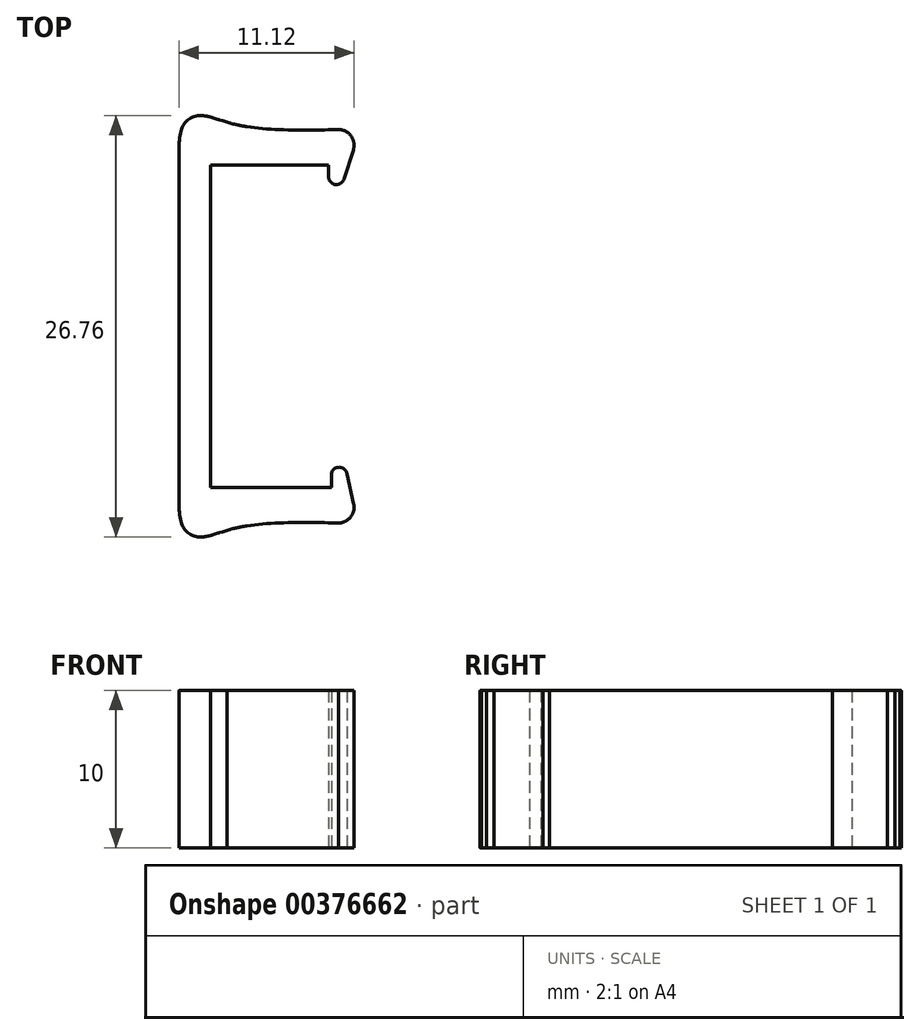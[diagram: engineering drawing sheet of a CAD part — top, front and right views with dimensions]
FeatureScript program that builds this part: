
annotation { "Feature Type Name" : "Feature", "Feature Type Description" : "" }
export const myFeature = defineFeature(function(context is Context, id is Id, definition is map)
    precondition{}
    {
        {
            var Q0;
            Q0=qCreatedBy(makeId("Top.planeOp"),FACE);
            var sketch = newSketch(context, id + "F0", { "sketchPlane" : qUnion([Q0])});
            skLineSegment(sketch, "E0.right", {"start": v(-6, 11) * mm, "end": v(-6, -11) * mm});
            skLineSegment(sketch, "E1.2", {"start": v(3.68, -10.25) * mm, "end": v(-4, -10.25) * mm});
            skLineSegment(sketch, "E1.3", {"start": v(-4, 10.25) * mm, "end": v(-4, -10.25) * mm});
            skLineSegment(sketch, "E2", {"start": v(3.5, 10.25) * mm, "end": v(3.5, 9.5) * mm});
            skArc(sketch, "E3.filletArc", {"start": v(3.5, 9.5) * mm, "mid": v(3.92, 9) * mm, "end": v(4.48, 9.35) * mm});
            skLineSegment(sketch, "E4", {"start": v(4.48, 9.35) * mm, "end": v(5.07, 11.2) * mm});
            skLineSegment(sketch, "E5.trimOffspring", {"start": v(3.5, 10.25) * mm, "end": v(-4, 10.25) * mm});
            skArc(sketch, "E6.MirrorCS", {"start": v(3.68, -9.5) * mm, "mid": v(4.12, -8.96) * mm, "end": v(4.68, -9.39) * mm});
            skLineSegment(sketch, "E7.MirrorCS", {"start": v(3.68, -10.25) * mm, "end": v(3.68, -9.5) * mm});
            skLineSegment(sketch, "E8.MirrorCS", {"start": v(4.68, -9.39) * mm, "end": v(5.1, -11.28) * mm});
            skPoint(sketch, "E9.visualSharp", {"position": v(5.37, -12.5) * mm});
            skArc(sketch, "E9.filletArc", {"start": v(4.12, -12.5) * mm, "mid": v(4.9, -12.13) * mm, "end": v(5.1, -11.28) * mm});
            skPoint(sketch, "E10.visualSharp", {"position": v(5.5, 12.5) * mm});
            skArc(sketch, "E10.filletArc", {"start": v(5.07, 11.2) * mm, "mid": v(4.93, 12.09) * mm, "end": v(4.12, 12.5) * mm});
            skPoint(sketch, "E11.visualSharp", {"position": v(-6, 12.5) * mm});
            skPoint(sketch, "E12.visualSharp", {"position": v(-6, -12.5) * mm});
            skLineSegment(sketch, "E13", {"start": v(-4, 10.25) * mm, "end": v(3.68, -10.25) * mm, "construction": true});
            skLineSegment(sketch, "E14", {"start": v(3.5, 10.25) * mm, "end": v(-4, -10.25) * mm, "construction": true});
            skLineSegment(sketch, "E15", {"start": v(0, 0) * mm, "end": v(7.63, 0) * mm, "construction": true});
            skFitSpline(sketch, "E16", {"points": [v(-6, 11) * mm, v(-5.67, 12.86) * mm, v(-4.63, 13.38) * mm, v(-2.08, 12.75) * mm, v(4.12, 12.5) * mm], "startDerivative": vector(0.04, 10.94) * mm, "endDerivative": vector(13.03, 0.4) * mm});
            skArc(sketch, "E17", {"start": v(-4.58, 13.38) * mm, "mid": v(-4.63, 13.43) * mm, "end": v(-4.68, 13.38) * mm});
            skArc(sketch, "E18", {"start": v(-4.28, 13.35) * mm, "mid": v(-4.32, 13.4) * mm, "end": v(-4.38, 13.37) * mm});
            skArc(sketch, "E19", {"start": v(-3.99, 13.29) * mm, "mid": v(-4.02, 13.35) * mm, "end": v(-4.08, 13.31) * mm});
            skArc(sketch, "E20", {"start": v(-3.7, 13.2) * mm, "mid": v(-3.73, 13.26) * mm, "end": v(-3.8, 13.23) * mm});
            skArc(sketch, "E21", {"start": v(-3.41, 13.11) * mm, "mid": v(-3.45, 13.17) * mm, "end": v(-3.5, 13.14) * mm});
            skArc(sketch, "E22", {"start": v(-3.13, 13.02) * mm, "mid": v(-3.16, 13.08) * mm, "end": v(-3.22, 13.05) * mm});
            skArc(sketch, "E23", {"start": v(-2.84, 12.94) * mm, "mid": v(-2.87, 13) * mm, "end": v(-2.94, 12.96) * mm});
            skArc(sketch, "E24", {"start": v(-2.55, 12.86) * mm, "mid": v(-2.59, 12.92) * mm, "end": v(-2.65, 12.88) * mm});
            skArc(sketch, "E25", {"start": v(-2.26, 12.79) * mm, "mid": v(-2.3, 12.85) * mm, "end": v(-2.36, 12.8) * mm});
            skArc(sketch, "E26", {"start": v(-1.96, 12.73) * mm, "mid": v(-2, 12.79) * mm, "end": v(-2.06, 12.75) * mm});
            skArc(sketch, "E27", {"start": v(-1.66, 12.68) * mm, "mid": v(-1.7, 12.73) * mm, "end": v(-1.76, 12.7) * mm});
            skArc(sketch, "E28.MirrorCS", {"start": v(-1.96, -12.73) * mm, "mid": v(-2, -12.79) * mm, "end": v(-2.06, -12.75) * mm});
            skArc(sketch, "E29.MirrorCS", {"start": v(-2.26, -12.79) * mm, "mid": v(-2.3, -12.85) * mm, "end": v(-2.36, -12.8) * mm});
            skFitSpline(sketch, "E30.MirrorCS", {"points": [v(-6, -11) * mm, v(-5.67, -12.86) * mm, v(-4.63, -13.38) * mm, v(-2.08, -12.75) * mm, v(4.12, -12.5) * mm], "startDerivative": vector(0.04, -10.94) * mm, "endDerivative": vector(13.03, -0.4) * mm});
            skArc(sketch, "E31.MirrorCS", {"start": v(-1.66, -12.68) * mm, "mid": v(-1.7, -12.73) * mm, "end": v(-1.76, -12.7) * mm});
            skArc(sketch, "E32.MirrorCS", {"start": v(-4.58, -13.38) * mm, "mid": v(-4.63, -13.43) * mm, "end": v(-4.68, -13.38) * mm});
            skArc(sketch, "E33.MirrorCS", {"start": v(-4.28, -13.35) * mm, "mid": v(-4.32, -13.4) * mm, "end": v(-4.38, -13.37) * mm});
            skFitSpline(sketch, "E34.MirrorCS", {"points": [v(-6, -11) * mm, v(-5.67, -12.86) * mm, v(-4.63, -13.38) * mm, v(-2.08, -12.75) * mm, v(4.12, -12.5) * mm], "startDerivative": vector(0.04, -10.94) * mm, "endDerivative": vector(13.03, -0.4) * mm});
            skArc(sketch, "E35.MirrorCS", {"start": v(-3.99, -13.29) * mm, "mid": v(-4.02, -13.35) * mm, "end": v(-4.08, -13.31) * mm});
            skArc(sketch, "E36.MirrorCS", {"start": v(-2.55, -12.86) * mm, "mid": v(-2.59, -12.92) * mm, "end": v(-2.65, -12.88) * mm});
            skArc(sketch, "E37.MirrorCS", {"start": v(-2.84, -12.94) * mm, "mid": v(-2.87, -13) * mm, "end": v(-2.94, -12.96) * mm});
            skArc(sketch, "E38.MirrorCS", {"start": v(-3.7, -13.2) * mm, "mid": v(-3.73, -13.26) * mm, "end": v(-3.8, -13.23) * mm});
            skArc(sketch, "E39.MirrorCS", {"start": v(-3.13, -13.02) * mm, "mid": v(-3.16, -13.08) * mm, "end": v(-3.22, -13.05) * mm});
            skArc(sketch, "E40.MirrorCS", {"start": v(-3.41, -13.11) * mm, "mid": v(-3.45, -13.17) * mm, "end": v(-3.5, -13.14) * mm});
            skFitSpline(sketch, "E41.MirrorCS", {"points": [v(-6, -11) * mm, v(-5.67, -12.86) * mm, v(-4.63, -13.38) * mm, v(-2.08, -12.75) * mm, v(4.12, -12.5) * mm], "startDerivative": vector(0.04, -10.94) * mm, "endDerivative": vector(13.03, -0.4) * mm});
            skSolve(sketch);
        }
        {
            var Q0;
            {var subQ1=sQuery(id+"F0.wireOp",EDGE,"E0.right");Q0=makeQuery(id+"F0.imprint","IMPRINT",FACE,{"disambiguationData":[TD([[makeQuery(id+"F0.imprint","IMPRINT",EDGE,{"derivedFrom":subQ1}),1.0]])]});}
            extrude(context, id + "F1", {"entities" : qUnion([Q0]), "depth" : 10 * mm, "offsetDistance" : 25 * mm});
        }
    });
